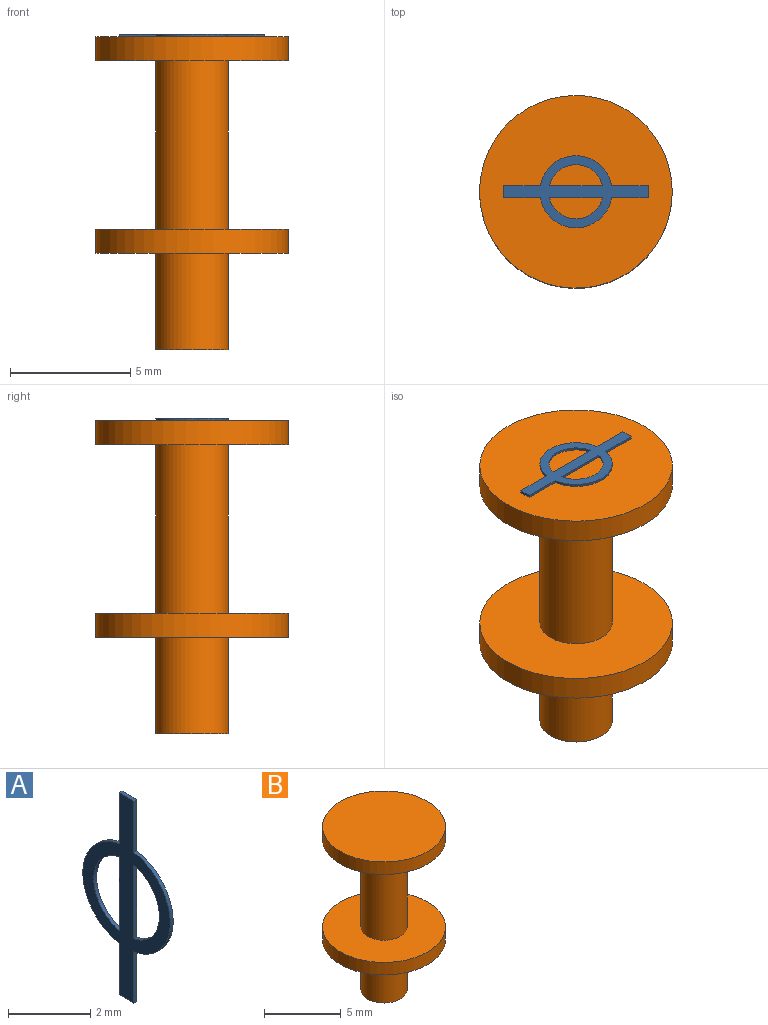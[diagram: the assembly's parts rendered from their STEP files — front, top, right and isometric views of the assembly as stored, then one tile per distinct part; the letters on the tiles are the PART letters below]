
ASSEMBLY  parts=2 mates=1
PART A: 14 faces, bbox 0.1x3x6 mm
  f0: plane 2.19x0.1mm, normal (0,-1,0), area 0.2mm2, adj f11,f12,f13
  f1: plane 2.19x0.1mm, normal (0,1,0), area 0.2mm2, adj f9,f12,f13
  f2: cylinder r=1.5mm len=2.96mm, axis (1,0,0), area 0.4mm2, adj f3,f10,f12,f13
  f3: plane 1.52x0.1mm, normal (0,1,0), area 0.2mm2, adj f2,f4,f12,f13
  f4: plane 0.5x0.1mm, normal (0,0,-1), area 0.1mm2, adj f3,f5,f12,f13
  f5: plane 1.52x0.1mm, normal (0,-1,0), area 0.2mm2, adj f4,f6,f12,f13
  f6: cylinder r=1.5mm len=2.96mm, axis (1,0,0), area 0.4mm2, adj f5,f7,f12,f13
  f7: plane 1.52x0.1mm, normal (0,-1,0), area 0.2mm2, adj f6,f8,f12,f13
  f8: plane 0.5x0.1mm, normal (0,0,1), area 0.1mm2, adj f7,f10,f12,f13
  f9: cylinder r=1.12mm len=2.19mm, axis (1,0,0), area 0.3mm2, adj f1,f12,f13
  f10: plane 1.52x0.1mm, normal (0,1,0), area 0.2mm2, adj f2,f8,f12,f13
  f11: cylinder r=1.12mm len=2.19mm, axis (1,0,0), area 0.3mm2, adj f0,f12,f13
  f12: plane 6x3mm, normal (-1,0,0), area 5.7mm2, adj f0,f1,f2,f3,f4,f5,f6,f7
  f13: plane 6x3mm, normal (1,0,0), area 5.7mm2, adj f0,f1,f2,f3,f4,f5,f6,f7
PART B: 9 faces, bbox 8x8x13 mm
  f0: plane 3x3mm, normal (0,0,-1), area 7.1mm2, adj f1
  f1: cylinder r=1.5mm len=4mm, axis (0,0,1), area 37.7mm2, adj f0,f2
  f2: plane 8x8mm, normal (0,0,-1), area 43.2mm2, adj f1,f3
  f3: cylinder r=4mm len=8mm, axis (0,0,1), area 25.1mm2, adj f2,f4
  f4: plane 8x8mm, normal (0,0,1), area 43.2mm2, adj f3,f5
  f5: cylinder r=1.5mm len=7mm, axis (0,0,1), area 66mm2, adj f4,f6
  f6: plane 8x8mm, normal (0,0,-1), area 43.2mm2, adj f5,f7
  f7: cylinder r=4mm len=8mm, axis (0,0,1), area 25.1mm2, adj f6,f8
  f8: plane 8x8mm, normal (0,0,1), area 50.3mm2, adj f7
PLACE A rot(axis=(0,1,0),90deg) t=(-14.14,0,-58.7)mm
PLACE B at identity
MATE planar A.f2 <-> B.f1  axis (0,0,-1) through (0,0,13)mm
